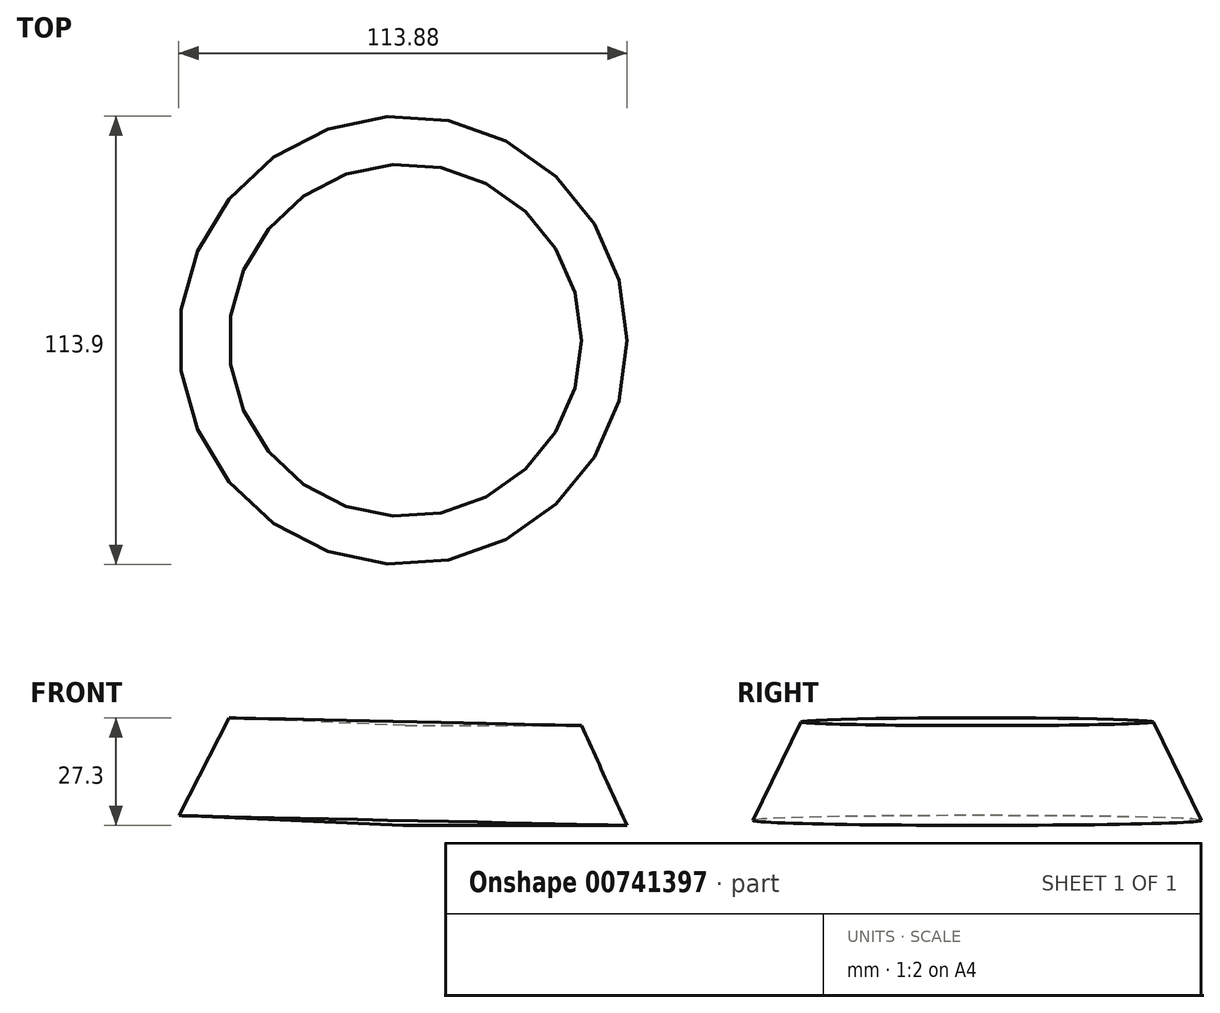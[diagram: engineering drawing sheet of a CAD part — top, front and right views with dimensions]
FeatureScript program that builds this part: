
annotation { "Feature Type Name" : "Feature", "Feature Type Description" : "" }
export const myFeature = defineFeature(function(context is Context, id is Id, definition is map)
    precondition{}
    {
        {
            var Q0;
            Q0=qCreatedBy(makeId("Front.planeOp"),FACE);
            var sketch = newSketch(context, id + "F0", { "sketchPlane" : qUnion([Q0])});
            skLineSegment(sketch, "E0", {"start": v(-24.43, 0) * mm, "end": v(32.54, 0) * mm});
            skLineSegment(sketch, "E1", {"start": v(32.54, 0) * mm, "end": v(20.92, 25.35) * mm});
            skLineSegment(sketch, "E2", {"start": v(20.92, 25.35) * mm, "end": v(-23.87, 25.35) * mm});
            skLineSegment(sketch, "E3", {"start": v(-23.87, 25.35) * mm, "end": v(-24.43, 0) * mm});
            skSolve(sketch);
        }
        {
            var Q0;
            Q0=makeQuery(id+"F0.imprint","IMPRINT",FACE,{"disambiguationData":[TD([[makeQuery(id+"F0.imprint","IMPRINT",EDGE,{"derivedFrom":sQuery(id+"F0.wireOp",EDGE,"E0")}),1.0]])]});
            var Q1;
            Q1=sQuery(id+"F0.wireOp",EDGE,"E3");
            revolve(context, id + "F1", {"surfaceOperationType" : NewSurfaceOperationType.NEW, "entities" : qUnion([Q0]), "axis" : qUnion([Q1]), "revolveType" : RevolveType.FULL});
        }
    });
